AUTODESK INVENTOR PART (.ipt)
format: ipt  version: 2016 (Build 200138000, 138)  size: 1,506,816 bytes
history: native  units: in
note: dims shown in document units (in); Inventor stores cm internally (conversion verified against a paired STEP export)
features: other x4, imported_body x4, sketch x1
ambient origin geometry x8: Origin, YZ Plane, XZ Plane, XY Plane, X Axis, Y Axis, Z Axis, Center Point
bodies: Body1 (feature_tree), Body2 (feature_tree), Body3 (feature_tree), Body4 (feature_tree)
feature tree (9):
  sketch  "Sketched Bend22"
  other  "usb double.ipt1"
  other  "Cut-Extrude5"
  other  "Cut-Extrude8"
  other  "Edge-Flange41"
  imported_body  "Base1"
  imported_body  "Base2"
  imported_body  "Base3"
  imported_body  "Base4"
